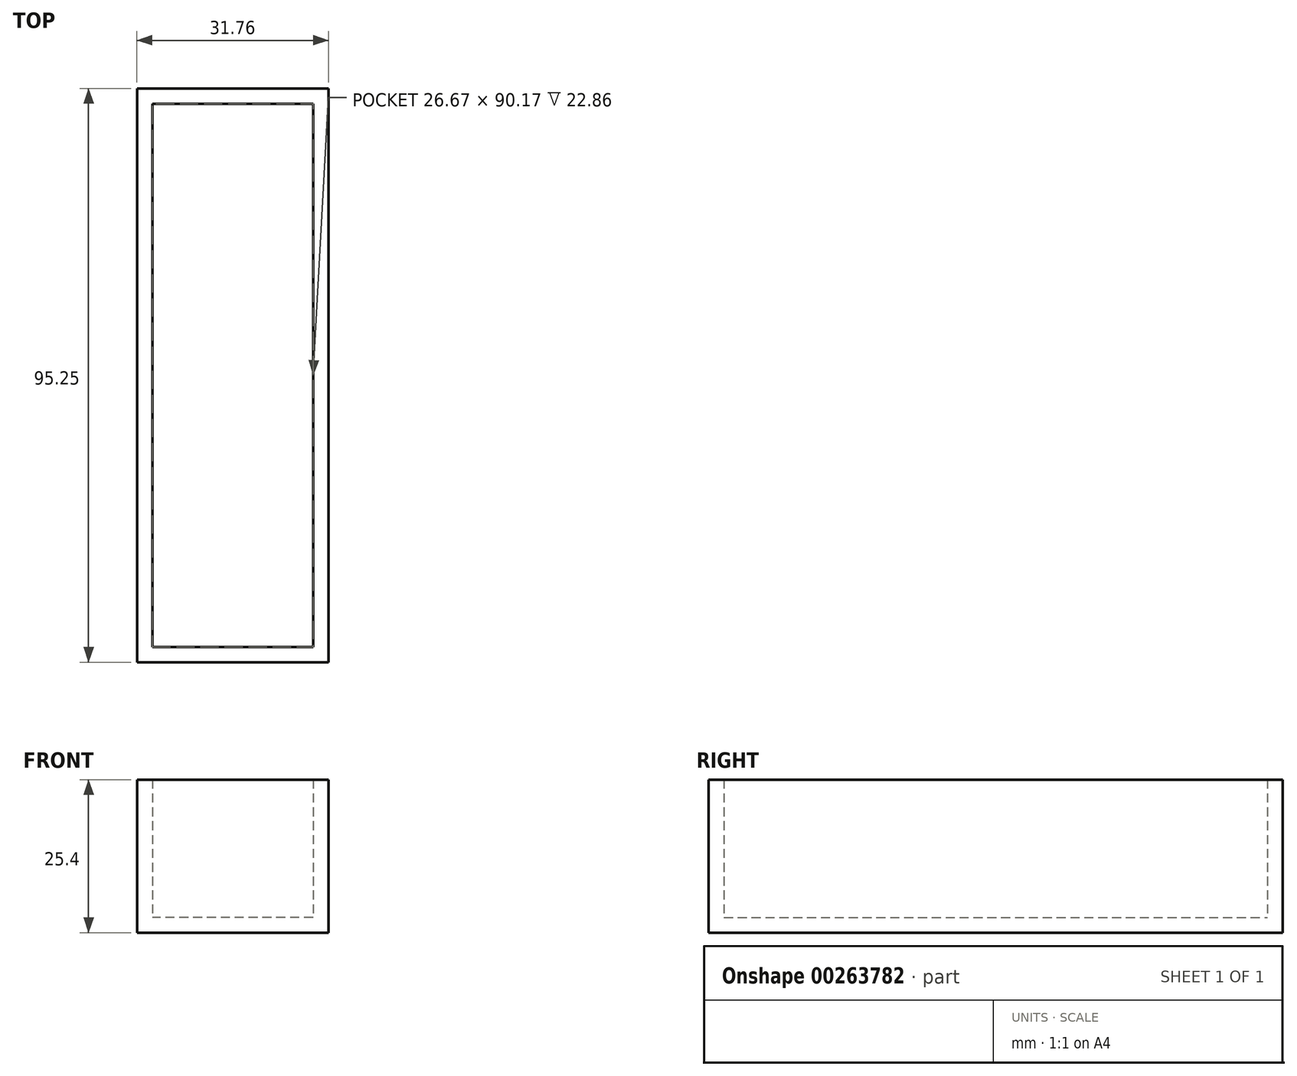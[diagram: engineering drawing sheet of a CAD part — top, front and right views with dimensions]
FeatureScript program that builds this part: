
annotation { "Feature Type Name" : "Feature", "Feature Type Description" : "" }
export const myFeature = defineFeature(function(context is Context, id is Id, definition is map)
    precondition{}
    {
        {
            var Q0;
            Q0=qCreatedBy(makeId("Front.planeOp"),FACE);
            var sketch = newSketch(context, id + "F0", { "sketchPlane" : qUnion([Q0])});
            skLineSegment(sketch, "E0.bottom", {"start": v(15.88, 12.7) * mm, "end": v(-15.88, 12.7) * mm});
            skLineSegment(sketch, "E0.top", {"start": v(15.88, -12.7) * mm, "end": v(-15.88, -12.7) * mm});
            skLineSegment(sketch, "E0.left", {"start": v(15.88, 12.7) * mm, "end": v(15.88, -12.7) * mm});
            skLineSegment(sketch, "E0.right", {"start": v(-15.88, 12.7) * mm, "end": v(-15.88, -12.7) * mm});
            skPoint(sketch, "E0.middle", {"position": v(0, 0) * mm});
            skSolve(sketch);
        }
        {
            var Q0;
            Q0 = qSketchRegion(id + "F0", true);
            extrude(context, id + "F1", {"entities" : qUnion([Q0]), "depth" : 95.25 * mm});
        }
        {
            var Q0;
            Q0=makeQuery(id+"F1.opExtrude","SWEPT_FACE",FACE,{"disambiguationData":[OSD([sQuery(id+"F0.wireOp",EDGE,"E0.bottom")])]});
            shell(context, id + "F2", {"entities" : qUnion([Q0]), "thickness" : 2.54 * mm});
        }
    });
